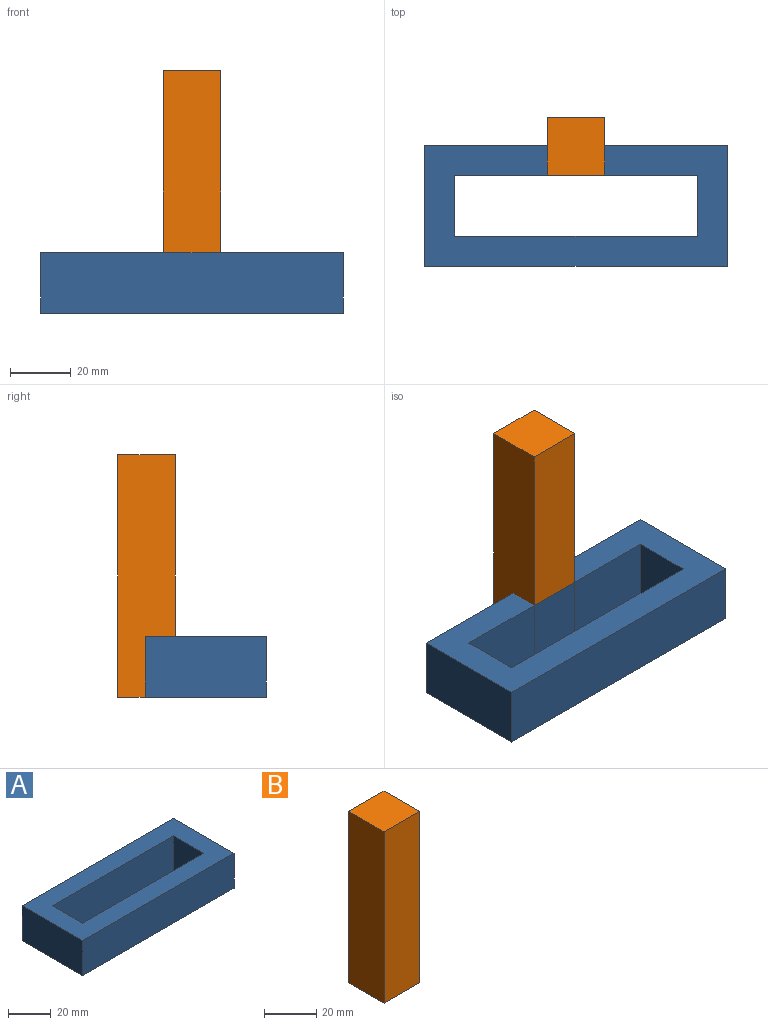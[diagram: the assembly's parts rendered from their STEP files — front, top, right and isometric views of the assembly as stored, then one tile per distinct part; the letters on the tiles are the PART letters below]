
ASSEMBLY  parts=2 mates=2
PART A: 10 faces, bbox 100x40x20 mm
  f0: plane 100x20mm, normal (0,-1,0), area 2000mm2, adj f1,f7,f8,f9
  f1: plane 40x20mm, normal (1,0,0), area 800mm2, adj f0,f2,f8,f9
  f2: plane 100x20mm, normal (0,1,0), area 2000mm2, adj f1,f7,f8,f9
  f3: plane 20x20mm, normal (-1,0,0), area 400mm2, adj f4,f6,f8,f9
  f4: plane 80x20mm, normal (0,1,0), area 1600mm2, adj f3,f5,f8,f9
  f5: plane 20x20mm, normal (1,0,0), area 400mm2, adj f4,f6,f8,f9
  f6: plane 80x20mm, normal (0,-1,0), area 1600mm2, adj f3,f5,f8,f9
  f7: plane 40x20mm, normal (-1,0,0), area 800mm2, adj f0,f2,f8,f9
  f8: plane 100x40mm, normal (0,0,1), area 2400mm2, adj f0,f1,f2,f3,f4,f5,f6,f7
  f9: plane 100x40mm, normal (0,0,-1), area 2400mm2, adj f0,f1,f2,f3,f4,f5,f6,f7
PART B: 6 faces, bbox 19x19x80 mm
  f0: plane 80x19mm, normal (0,1,0), area 1520mm2, adj f1,f3,f4,f5
  f1: plane 80x19mm, normal (-1,0,0), area 1520mm2, adj f0,f2,f4,f5
  f2: plane 80x19mm, normal (0,-1,0), area 1520mm2, adj f1,f3,f4,f5
  f3: plane 80x19mm, normal (1,0,0), area 1520mm2, adj f0,f2,f4,f5
  f4: plane 19x19mm, normal (0,0,1), area 361mm2, adj f0,f1,f2,f3
  f5: plane 19x19mm, normal (0,0,-1), area 361mm2, adj f0,f1,f2,f3
PLACE A t=(37.15,-45.26,21.9)mm fixed
PLACE B rot(axis=(0,0,1),90deg) t=(37.36,-0.78,21.9)mm
MATE parallel B.f1 <-> A.f6  axis (0,-1,0) through (37.15,-35.26,61.9)mm
MATE planar B.f5 <-> A.f9  axis (0,0,-1) through (37.15,-25.76,21.9)mm
